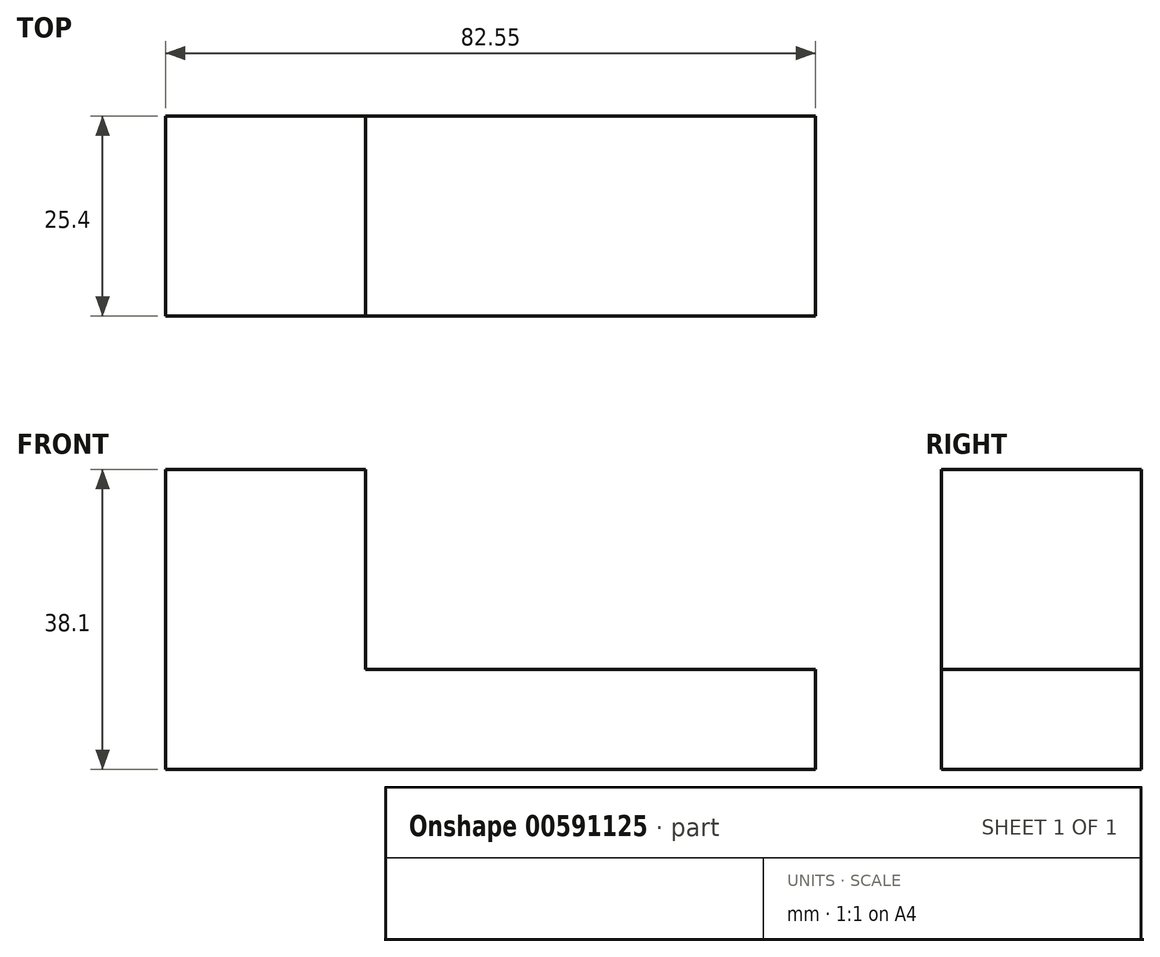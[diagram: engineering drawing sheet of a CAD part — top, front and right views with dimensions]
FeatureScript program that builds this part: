
annotation { "Feature Type Name" : "Feature", "Feature Type Description" : "" }
export const myFeature = defineFeature(function(context is Context, id is Id, definition is map)
    precondition{}
    {
        {
            var Q0;
            Q0=qCreatedBy(makeId("Front.planeOp"),FACE);
            var sketch = newSketch(context, id + "F0", { "sketchPlane" : qUnion([Q0])});
            skLineSegment(sketch, "E0", {"start": v(0, 0) * mm, "end": v(0, 38.1) * mm});
            skLineSegment(sketch, "E1", {"start": v(0, 38.1) * mm, "end": v(25.4, 38.1) * mm});
            skLineSegment(sketch, "E2", {"start": v(25.4, 38.1) * mm, "end": v(25.4, 12.7) * mm});
            skLineSegment(sketch, "E3", {"start": v(25.4, 12.7) * mm, "end": v(82.55, 12.7) * mm});
            skLineSegment(sketch, "E4", {"start": v(82.55, 0) * mm, "end": v(82.55, 12.7) * mm});
            skLineSegment(sketch, "E5", {"start": v(82.55, 0) * mm, "end": v(0, 0) * mm});
            skSolve(sketch);
        }
        {
            var Q0;
            Q0=makeQuery(id+"F0.imprint","IMPRINT",FACE,{"disambiguationData":[TD([[makeQuery(id+"F0.imprint","IMPRINT",EDGE,{"derivedFrom":sQuery(id+"F0.wireOp",EDGE,"E0")}),-1.0]])]});
            extrude(context, id + "F1", {"entities" : qUnion([Q0]), "depth" : 25.4 * mm, "offsetDistance" : 25.4 * mm});
        }
    });
